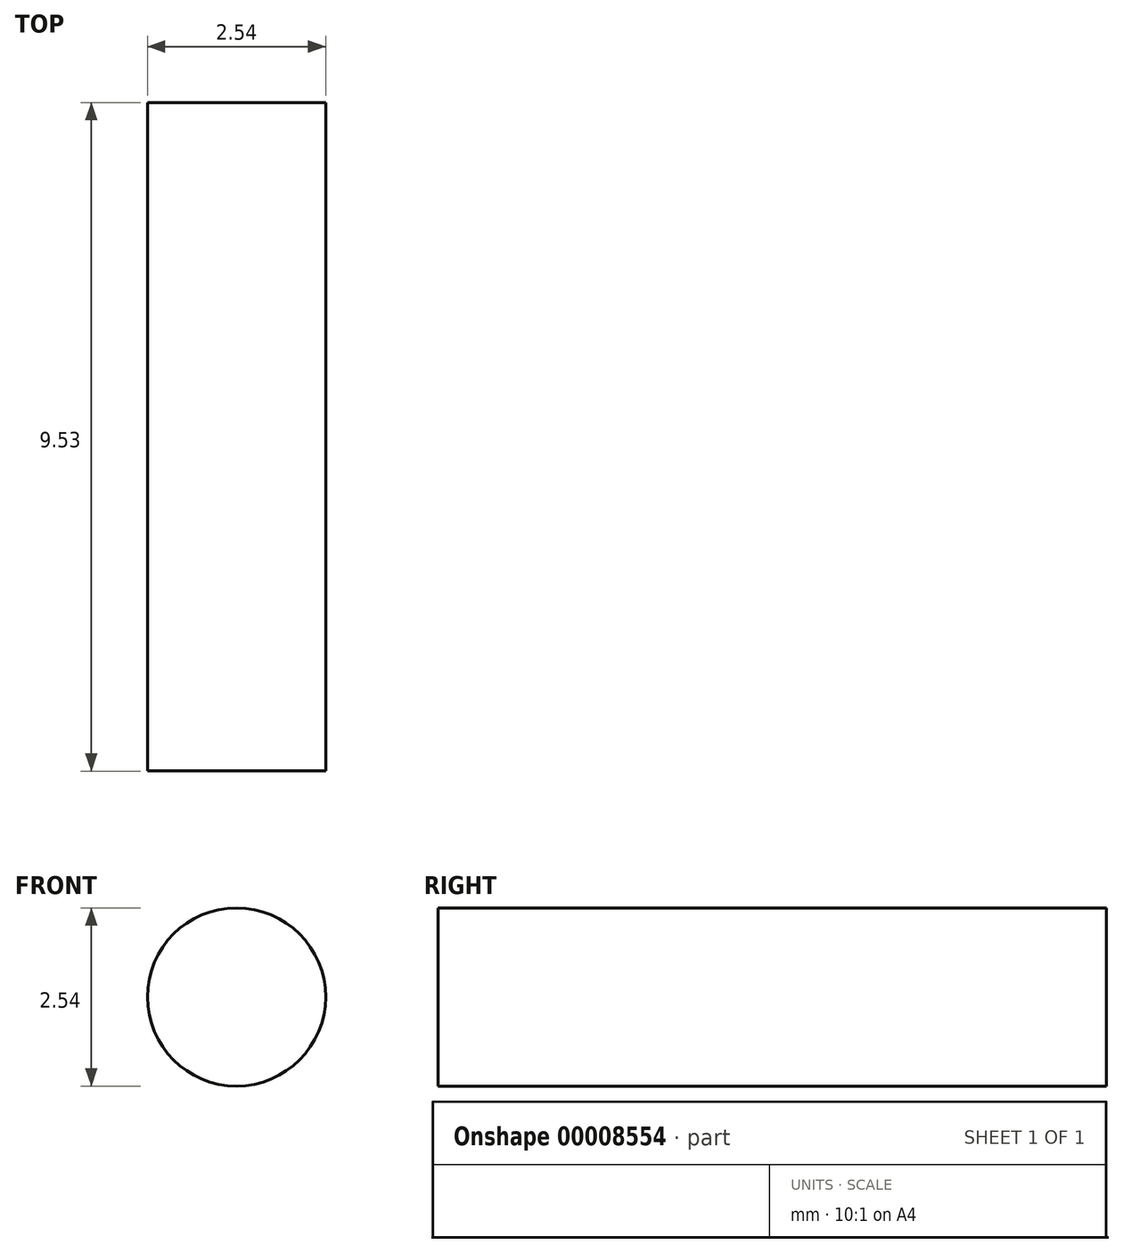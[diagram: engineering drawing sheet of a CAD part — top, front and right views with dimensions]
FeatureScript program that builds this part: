
annotation { "Feature Type Name" : "Feature", "Feature Type Description" : "" }
export const myFeature = defineFeature(function(context is Context, id is Id, definition is map)
    precondition{}
    {
        {
            var Q0;
            Q0=qCreatedBy(makeId("Front.planeOp"),FACE);
            var sketch = newSketch(context, id + "F0", { "sketchPlane" : qUnion([Q0])});
            skCircle(sketch, "E0", {"center": v(0, 0) * mm, "radius": 1.27 * mm});
            skSolve(sketch);
        }
        {
            var Q0;
            Q0=makeQuery(id+"F0.imprint","IMPRINT",FACE,{"disambiguationData":[TD([[makeQuery(id+"F0.imprint","IMPRINT",EDGE,{"derivedFrom":sQuery(id+"F0.wireOp",EDGE,"E0")}),1.0]])]});
            extrude(context, id + "F1", {"entities" : qUnion([Q0]), "depth" : 9.52 * mm});
        }
    });
